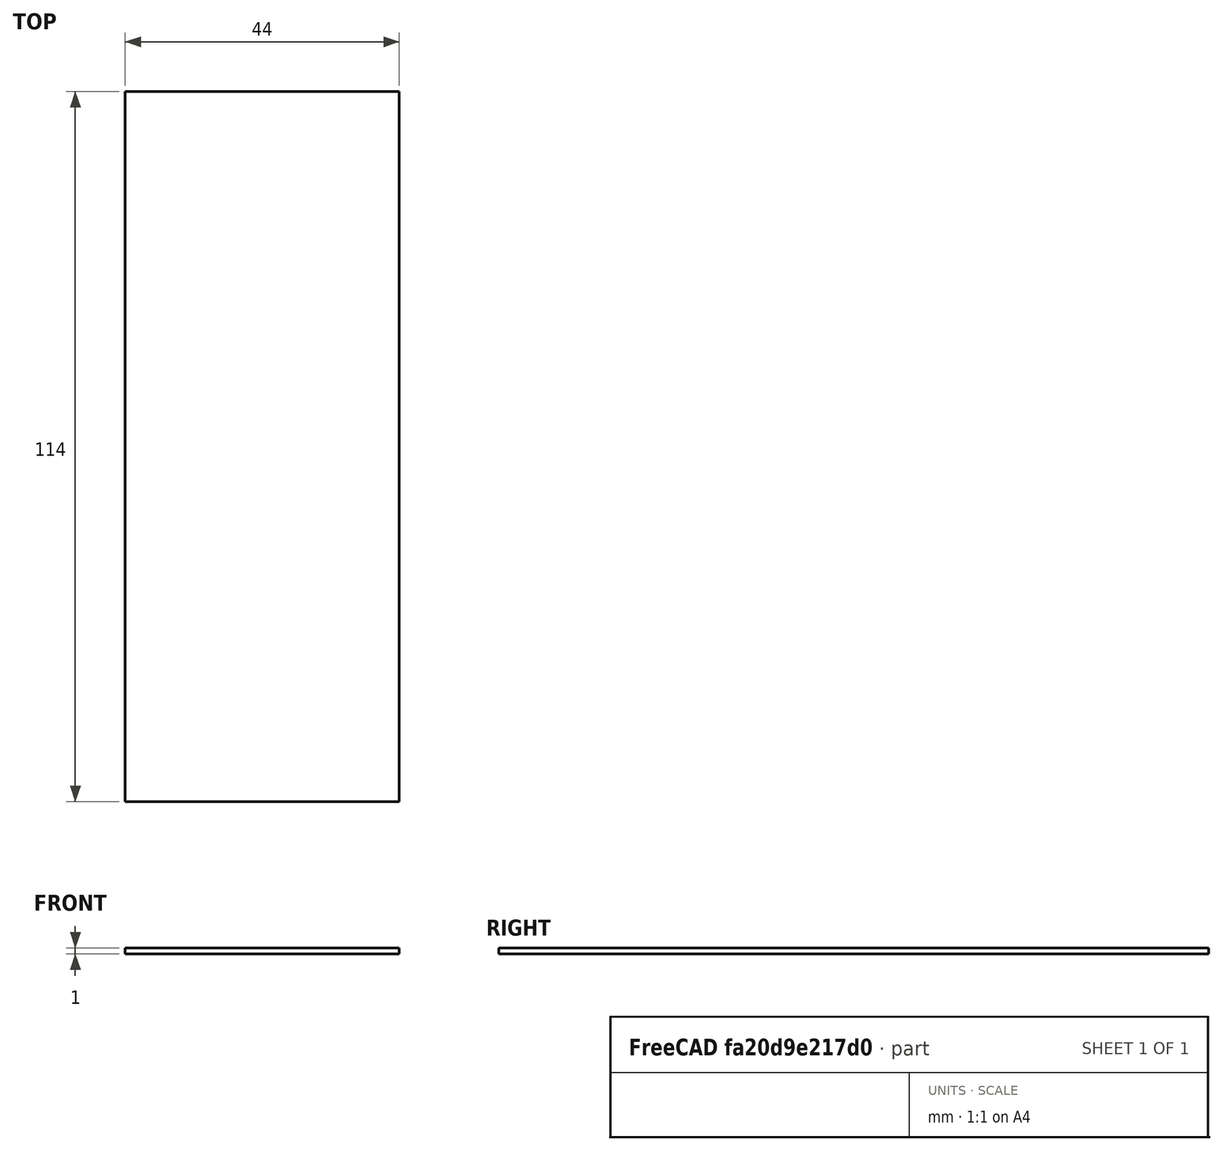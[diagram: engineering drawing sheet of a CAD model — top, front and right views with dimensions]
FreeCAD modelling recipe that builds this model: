
FCSTD DOCUMENT  (FreeCAD 0.18.4R)
Label: dyn-bg
License: All rights reserved
LicenseURL: http://en.wikipedia.org/wiki/All_rights_reserved
objects: Sketcher::SketchObject×1, PartDesign::Pad×1, PartDesign::Body×1
note: 4 computed .brp shape members not serialized (recipe doc carries the construction recipe); baked Part::Feature solids carry a one-line shape summary decoded from their .brp

FEATURE [Sketcher::SketchObject] Sketch
  MapMode = 5
  Support = -> [XY_Plane]
  sketch-geometry (4):
    g0: LineSegment StartX=-22 StartY=114 StartZ=0 EndX=22 EndY=114 EndZ=0
    g1: LineSegment StartX=22 StartY=114 StartZ=0 EndX=22 EndY=0 EndZ=0
    g2: LineSegment StartX=22 StartY=0 StartZ=0 EndX=-22 EndY=0 EndZ=0
    g3: LineSegment StartX=-22 StartY=0 StartZ=0 EndX=-22 EndY=114 EndZ=0
  constraints (12):
    c: Coincident(g0,g1)
    c: Coincident(g1,g2)
    c: Coincident(g2,g3)
    c: Coincident(g3,g0)
    c: Horizontal(g0)
    c: Horizontal(g2)
    c: Vertical(g1)
    c: Vertical(g3)
    c: DistanceY(g3,g3) = 114
    c: DistanceX(g0,g0) = 44
    c: DistanceX(g0,g-1) = 22
    c: PointOnObject(g2,g-1)
FEATURE [PartDesign::Pad] Pad
  Length = 1
  Length2 = 100
  Profile = -> Sketch
  Type = 0
FEATURE [PartDesign::Body] Body
  Group = -> [Sketch,Pad]
  Origin = -> Origin
  Tip = -> Pad
